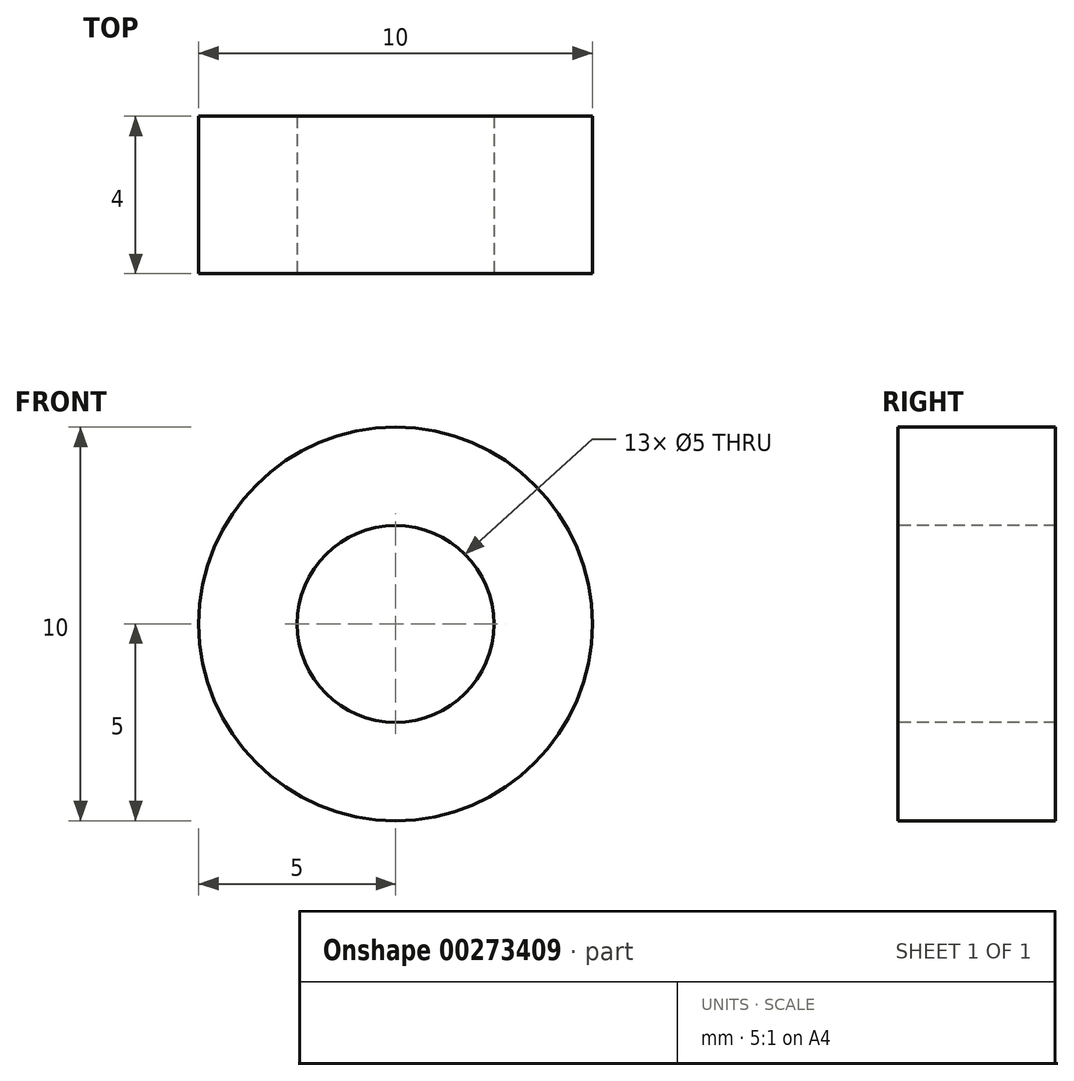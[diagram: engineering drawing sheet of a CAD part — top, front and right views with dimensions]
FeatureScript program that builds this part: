
annotation { "Feature Type Name" : "Feature", "Feature Type Description" : "" }
export const myFeature = defineFeature(function(context is Context, id is Id, definition is map)
    precondition{}
    {
        {
            var Q0;
            Q0=qCreatedBy(makeId("Right.planeOp"),FACE);
            var sketch = newSketch(context, id + "F0", { "sketchPlane" : qUnion([Q0])});
            skLineSegment(sketch, "E0.bottom", {"start": v(-2, 5) * mm, "end": v(2, 5) * mm});
            skLineSegment(sketch, "E0.top", {"start": v(-2, 2.5) * mm, "end": v(2, 2.5) * mm});
            skLineSegment(sketch, "E0.left", {"start": v(-2, 5) * mm, "end": v(-2, 2.5) * mm});
            skLineSegment(sketch, "E0.right", {"start": v(2, 5) * mm, "end": v(2, 2.5) * mm});
            skPoint(sketch, "E0.middle", {"position": v(0, 3.75) * mm});
            skSolve(sketch);
        }
        {
            var Q0;
            Q0=qCreatedBy(makeId("Top.planeOp"),FACE);
            var sketch = newSketch(context, id + "F1", { "sketchPlane" : qUnion([Q0])});
            skLineSegment(sketch, "E1", {"start": v(0, -7.37) * mm, "end": v(0, 9.85) * mm, "construction": true});
            skSolve(sketch);
        }
        {
            var Q0;
            Q0=makeQuery(id+"F0.imprint","IMPRINT",FACE,{"disambiguationData":[TD([[makeQuery(id+"F0.imprint","IMPRINT",EDGE,{"derivedFrom":sQuery(id+"F0.wireOp",EDGE,"E0.bottom")}),-1.0]])]});
            var Q1;
            Q1=sQuery(id+"F1.wireOp",EDGE,"E1");
            revolve(context, id + "F2", {"entities" : qUnion([Q0]), "axis" : qUnion([Q1]), "revolveType" : RevolveType.FULL});
        }
    });
